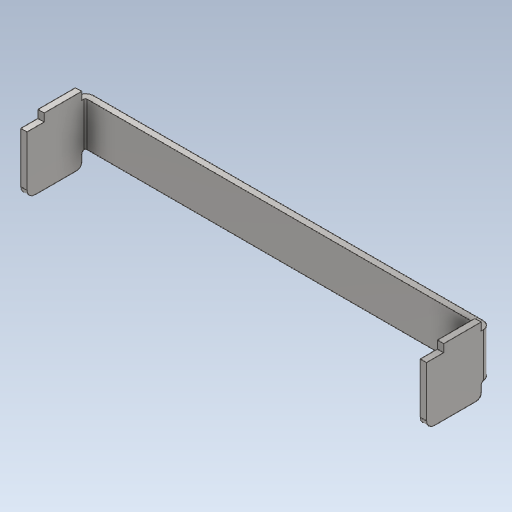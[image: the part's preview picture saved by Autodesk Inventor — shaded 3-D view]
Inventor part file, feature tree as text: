
AUTODESK INVENTOR PART (.ipt)
format: ipt  version: 2020 (Build 240168000, 168)  size: 291,328 bytes
history: native  units: mm
features: other x4, extrude x1
ambient origin geometry x8: Origin, YZ Plane, XZ Plane, XY Plane, X Axis, Y Axis, Z Axis, Center Point
bodies: Body1 (feature_tree)
feature tree (5):
  other  "實體1"
  extrude  "擠出1"  Depth=2.0mm TaperAngle=0.0deg
  other  "折彎零件1"
  other  "折彎零件2"
  other  "定義1"
